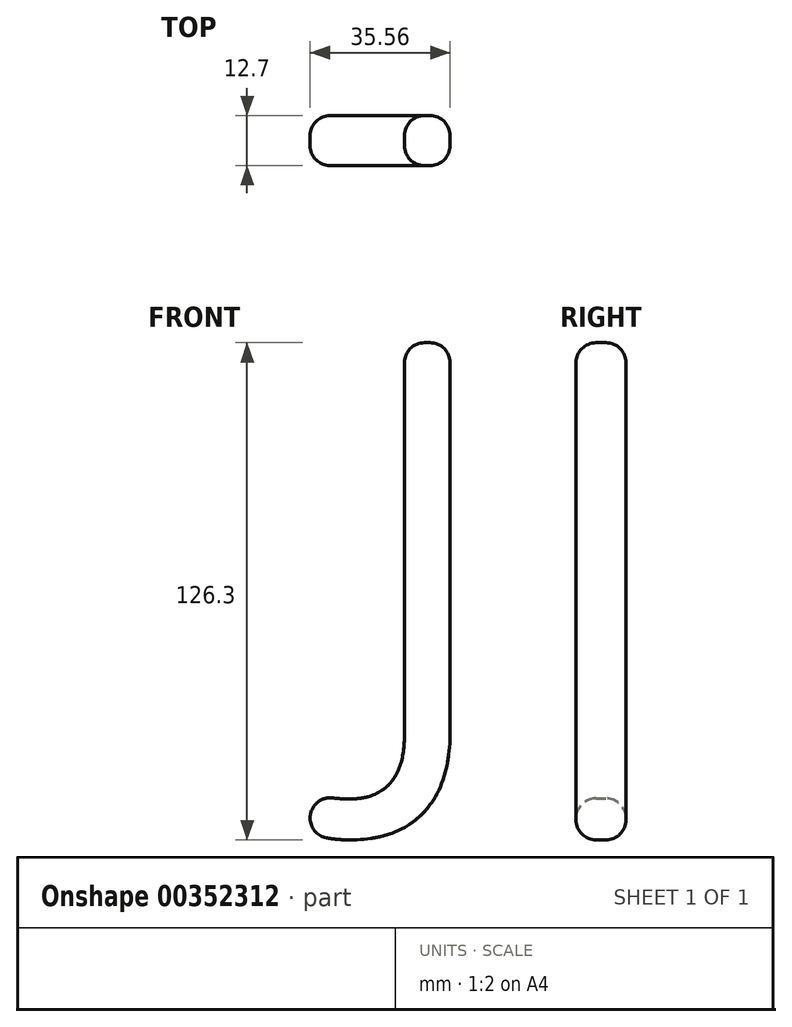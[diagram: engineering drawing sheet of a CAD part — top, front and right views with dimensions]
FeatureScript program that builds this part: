
annotation { "Feature Type Name" : "Feature", "Feature Type Description" : "" }
export const myFeature = defineFeature(function(context is Context, id is Id, definition is map)
    precondition{}
    {
        {
            var Q0;
            Q0=qCreatedBy(makeId("Front.planeOp"),FACE);
            var sketch = newSketch(context, id + "F0", { "sketchPlane" : qUnion([Q0])});
            skText(sketch, "E0", { "text": "J", "fontName": "OpenSans-Regular.ttf"});
            const initialGuessF0  = {"E0": [-0.01274, -0.02818, 1, 0, 0.10083]};
            skSetInitialGuess(sketch, initialGuessF0);
            skSolve(sketch);
        }
        {
            var Q0;
            Q0=makeQuery(id+"F0.imprint","IMPRINT",FACE,{"disambiguationData":[TD([[makeQuery(id+"F0.imprint","IMPRINT",EDGE,{"derivedFrom":sQuery(id+"F0.wireOp",EDGE,"E0.sketch_text.stroke-0")}),-1.0]])]});
            extrude(context, id + "F1", {"entities" : qUnion([Q0]), "depth" : 12.7 * mm});
        }
        {
            var Q0;
            Q0=makeQuery(id+"F1.opExtrude","CAP_EDGE",EDGE,{"disambiguationData":[OSD([sQuery(id+"F0.wireOp",EDGE,"E0.sketch_text.stroke-2")])],"isStart":false});
            var Q1;
            Q1=makeQuery(id+"F1.opExtrude","CAP_EDGE",EDGE,{"disambiguationData":[OSD([sQuery(id+"F0.wireOp",EDGE,"E0.sketch_text.stroke-0")])],"isStart":true});
            var Q2;
            Q2=makeQuery(id+"F1.opExtrude","CAP_EDGE",EDGE,{"disambiguationData":[OSD([sQuery(id+"F0.wireOp",EDGE,"E0.sketch_text.stroke-0")])],"isStart":false});
            var Q3;
            Q3=makeQuery(id+"F1.opExtrude","CAP_EDGE",EDGE,{"disambiguationData":[OSD([sQuery(id+"F0.wireOp",EDGE,"E0.sketch_text.stroke-9")])],"isStart":false});
            var Q4;
            Q4=makeQuery(id+"F1.opExtrude","CAP_EDGE",EDGE,{"disambiguationData":[OSD([sQuery(id+"F0.wireOp",EDGE,"E0.sketch_text.stroke-8")])],"isStart":true});
            var Q5;
            Q5=makeQuery(id+"F1.opExtrude","CAP_EDGE",EDGE,{"disambiguationData":[OSD([sQuery(id+"F0.wireOp",EDGE,"E0.sketch_text.stroke-8")])],"isStart":false});
            var Q6;
            Q6=makeQuery(id+"F1.opExtrude","CAP_EDGE",EDGE,{"disambiguationData":[OSD([sQuery(id+"F0.wireOp",EDGE,"E0.sketch_text.stroke-9")])],"isStart":true});
            var Q7;
            Q7=makeQuery(id+"F1.opExtrude","SWEPT_EDGE",EDGE,{"disambiguationData":[OSD([sQuery(id+"F0.wireOp",EDGE,"E0.sketch_text.stroke-0"),sQuery(id+"F0.wireOp",EDGE,"E0.sketch_text.stroke-1")])]});
            var Q8;
            Q8=makeQuery(id+"F1.opExtrude","SWEPT_EDGE",EDGE,{"disambiguationData":[OSD([sQuery(id+"F0.wireOp",EDGE,"E0.sketch_text.stroke-0"),sQuery(id+"F0.wireOp",EDGE,"E0.sketch_text.stroke-9")])]});
            var Q9;
            Q9=makeQuery(id+"F1.opExtrude","CAP_EDGE",EDGE,{"disambiguationData":[OSD([sQuery(id+"F0.wireOp",EDGE,"E0.sketch_text.stroke-2")])],"isStart":true});
            var Q10;
            Q10=makeQuery(id+"F1.opExtrude","CAP_EDGE",EDGE,{"disambiguationData":[OSD([sQuery(id+"F0.wireOp",EDGE,"E0.sketch_text.stroke-1")])],"isStart":false});
            var Q11;
            Q11=makeQuery(id+"F1.opExtrude","SWEPT_EDGE",EDGE,{"disambiguationData":[OSD([sQuery(id+"F0.wireOp",EDGE,"E0.sketch_text.stroke-7"),sQuery(id+"F0.wireOp",EDGE,"E0.sketch_text.stroke-8")])]});
            var Q12;
            Q12=makeQuery(id+"F1.opExtrude","SWEPT_EDGE",EDGE,{"disambiguationData":[OSD([sQuery(id+"F0.wireOp",EDGE,"E0.sketch_text.stroke-8"),sQuery(id+"F0.wireOp",EDGE,"E0.sketch_text.stroke-9")])]});
            var Q13;
            Q13=makeQuery(id+"F1.opExtrude","CAP_EDGE",EDGE,{"disambiguationData":[OSD([sQuery(id+"F0.wireOp",EDGE,"E0.sketch_text.stroke-3")])],"isStart":true});
            var Q14;
            Q14=makeQuery(id+"F1.opExtrude","CAP_EDGE",EDGE,{"disambiguationData":[OSD([sQuery(id+"F0.wireOp",EDGE,"E0.sketch_text.stroke-3")])],"isStart":false});
            var Q15;
            Q15=makeQuery(id+"F1.opExtrude","CAP_EDGE",EDGE,{"disambiguationData":[OSD([sQuery(id+"F0.wireOp",EDGE,"E0.sketch_text.stroke-4")])],"isStart":false});
            var Q16;
            Q16=makeQuery(id+"F1.opExtrude","CAP_EDGE",EDGE,{"disambiguationData":[OSD([sQuery(id+"F0.wireOp",EDGE,"E0.sketch_text.stroke-7")])],"isStart":false});
            var Q17;
            Q17=makeQuery(id+"F1.opExtrude","SWEPT_EDGE",EDGE,{"disambiguationData":[OSD([sQuery(id+"F0.wireOp",EDGE,"E0.sketch_text.stroke-3"),sQuery(id+"F0.wireOp",EDGE,"E0.sketch_text.stroke-4")])]});
            var Q18;
            Q18=makeQuery(id+"F1.opExtrude","SWEPT_EDGE",EDGE,{"disambiguationData":[OSD([sQuery(id+"F0.wireOp",EDGE,"E0.sketch_text.stroke-2"),sQuery(id+"F0.wireOp",EDGE,"E0.sketch_text.stroke-3")])]});
            var Q19;
            Q19=makeQuery(id+"F1.opExtrude","SWEPT_EDGE",EDGE,{"disambiguationData":[OSD([sQuery(id+"F0.wireOp",EDGE,"E0.sketch_text.stroke-1"),sQuery(id+"F0.wireOp",EDGE,"E0.sketch_text.stroke-2")])]});
            var Q20;
            Q20=makeQuery(id+"F1.opExtrude","SWEPT_EDGE",EDGE,{"disambiguationData":[OSD([sQuery(id+"F0.wireOp",EDGE,"E0.sketch_text.stroke-4"),sQuery(id+"F0.wireOp",EDGE,"E0.sketch_text.stroke-5")])]});
            var Q21;
            Q21=makeQuery(id+"F1.opExtrude","SWEPT_EDGE",EDGE,{"disambiguationData":[OSD([sQuery(id+"F0.wireOp",EDGE,"E0.sketch_text.stroke-5"),sQuery(id+"F0.wireOp",EDGE,"E0.sketch_text.stroke-6")])]});
            var Q22;
            Q22=makeQuery(id+"F1.opExtrude","SWEPT_EDGE",EDGE,{"disambiguationData":[OSD([sQuery(id+"F0.wireOp",EDGE,"E0.sketch_text.stroke-6"),sQuery(id+"F0.wireOp",EDGE,"E0.sketch_text.stroke-7")])]});
            var Q23;
            Q23=makeQuery(id+"F1.opExtrude","CAP_EDGE",EDGE,{"disambiguationData":[OSD([sQuery(id+"F0.wireOp",EDGE,"E0.sketch_text.stroke-1")])],"isStart":true});
            var Q24;
            Q24=makeQuery(id+"F1.opExtrude","CAP_EDGE",EDGE,{"disambiguationData":[OSD([sQuery(id+"F0.wireOp",EDGE,"E0.sketch_text.stroke-4")])],"isStart":true});
            var Q25;
            Q25=makeQuery(id+"F1.opExtrude","CAP_EDGE",EDGE,{"disambiguationData":[OSD([sQuery(id+"F0.wireOp",EDGE,"E0.sketch_text.stroke-5")])],"isStart":false});
            var Q26;
            Q26=makeQuery(id+"F1.opExtrude","CAP_EDGE",EDGE,{"disambiguationData":[OSD([sQuery(id+"F0.wireOp",EDGE,"E0.sketch_text.stroke-6")])],"isStart":true});
            var Q27;
            Q27=makeQuery(id+"F1.opExtrude","CAP_EDGE",EDGE,{"disambiguationData":[OSD([sQuery(id+"F0.wireOp",EDGE,"E0.sketch_text.stroke-6")])],"isStart":false});
            var Q28;
            Q28=makeQuery(id+"F1.opExtrude","CAP_EDGE",EDGE,{"disambiguationData":[OSD([sQuery(id+"F0.wireOp",EDGE,"E0.sketch_text.stroke-7")])],"isStart":true});
            var Q29;
            Q29=makeQuery(id+"F1.opExtrude","CAP_EDGE",EDGE,{"disambiguationData":[OSD([sQuery(id+"F0.wireOp",EDGE,"E0.sketch_text.stroke-5")])],"isStart":true});
            fillet(context, id + "F2", {"entities" : qUnion([Q0, Q1, Q2, Q3, Q4, Q5, Q6, Q7, Q8, Q9, Q10, Q11, Q12, Q13, Q14, Q15, Q16, Q17, Q18, Q19, Q20, Q21, Q22, Q23, Q24, Q25, Q26, Q27, Q28, Q29]), "radius" : 5.08 * mm, "tangentPropagation" : true, "allowEdgeOverflow" : false});
        }
    });
